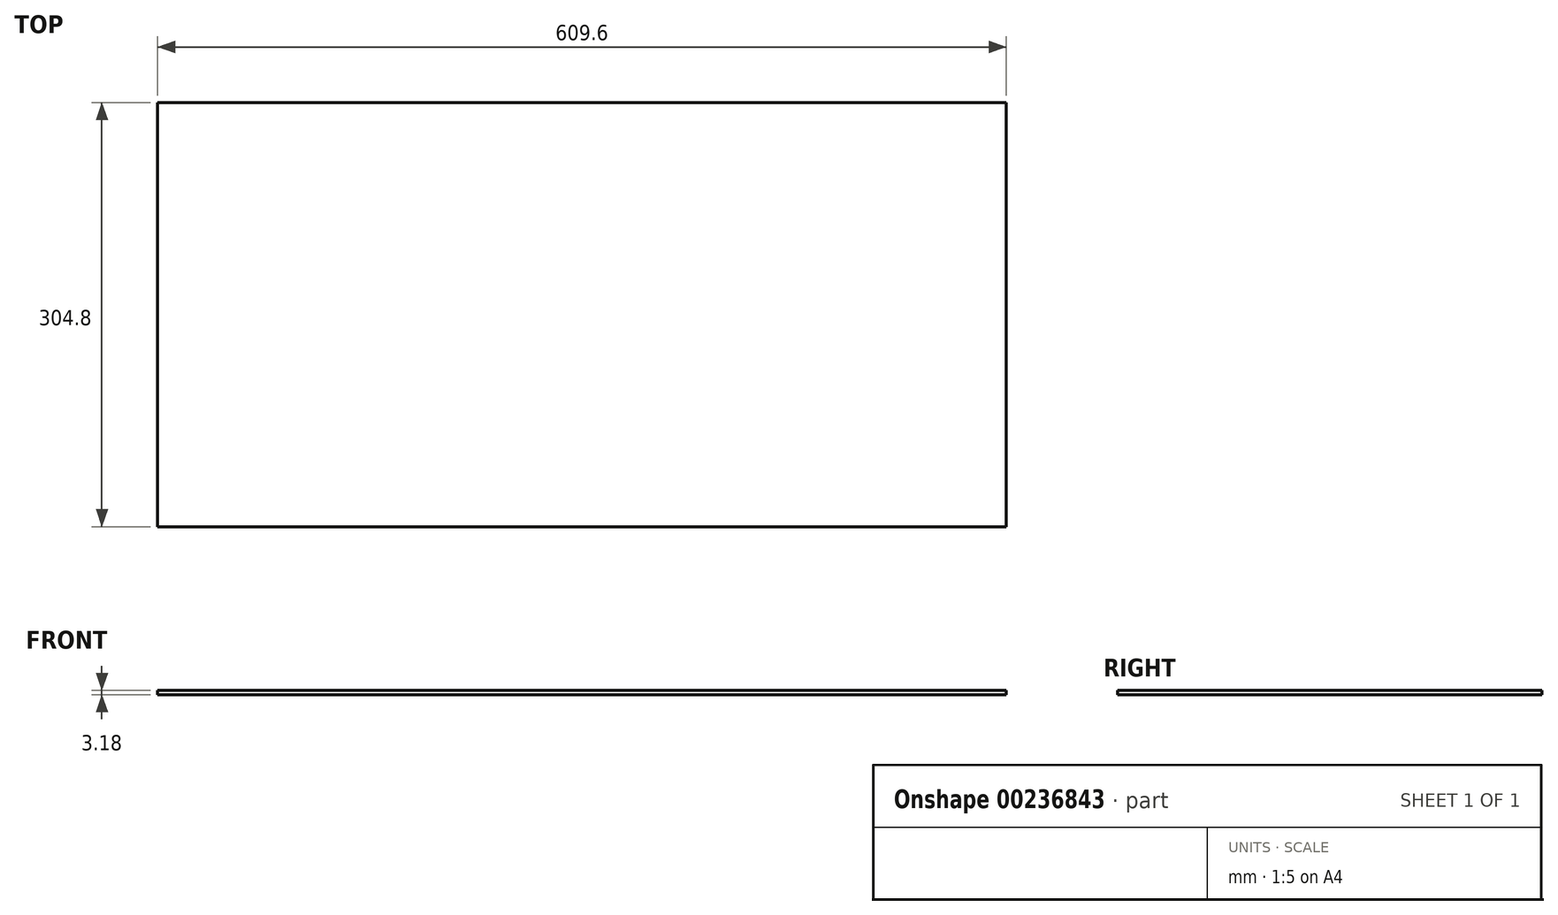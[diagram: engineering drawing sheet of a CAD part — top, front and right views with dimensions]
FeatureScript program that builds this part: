
annotation { "Feature Type Name" : "Feature", "Feature Type Description" : "" }
export const myFeature = defineFeature(function(context is Context, id is Id, definition is map)
    precondition{}
    {
        {
            var Q0;
            Q0=qCreatedBy(makeId("Top.planeOp"),FACE);
            var sketch = newSketch(context, id + "F0", { "sketchPlane" : qUnion([Q0])});
            skLineSegment(sketch, "E0.bottom", {"start": v(304.8, -152.4) * mm, "end": v(-304.8, -152.4) * mm});
            skLineSegment(sketch, "E0.top", {"start": v(304.8, 152.4) * mm, "end": v(-304.8, 152.4) * mm});
            skLineSegment(sketch, "E0.left", {"start": v(304.8, -152.4) * mm, "end": v(304.8, 152.4) * mm});
            skLineSegment(sketch, "E0.right", {"start": v(-304.8, -152.4) * mm, "end": v(-304.8, 152.4) * mm});
            skPoint(sketch, "E0.middle", {"position": v(0, 0) * mm});
            skSolve(sketch);
        }
        {
            var Q0;
            Q0=qSketchRegion(id+"F0",true);
            extrude(context, id + "F1", {"entities" : qUnion([Q0]), "endBound" : BoundingType.SYMMETRIC, "depth" : 3.17 * mm});
        }
    });
